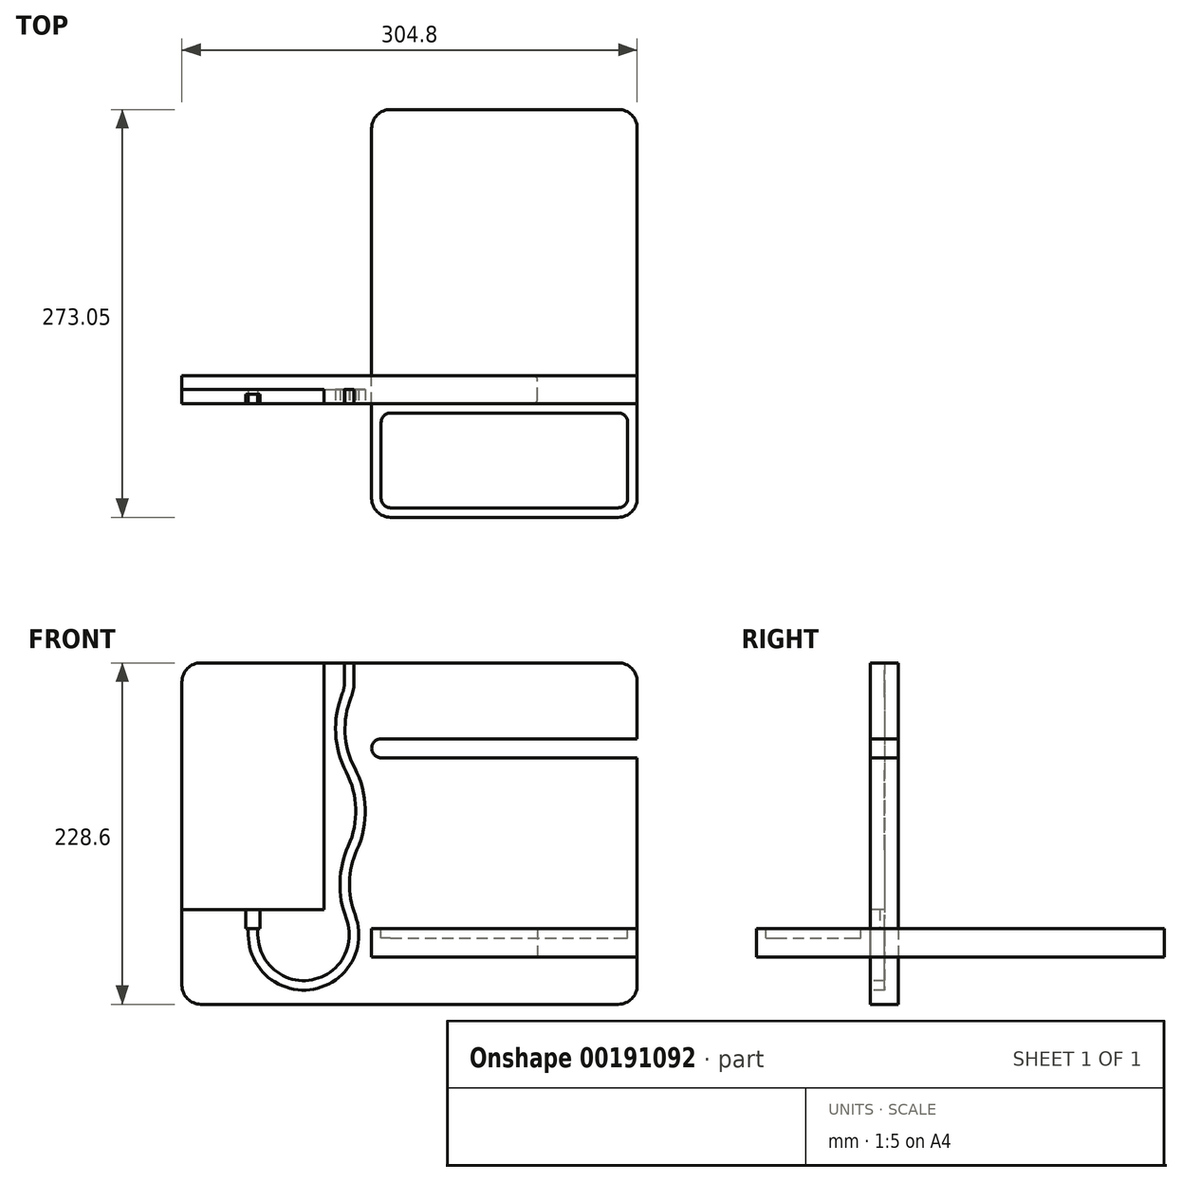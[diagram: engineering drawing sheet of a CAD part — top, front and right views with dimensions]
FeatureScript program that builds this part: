
annotation { "Feature Type Name" : "Feature", "Feature Type Description" : "" }
export const myFeature = defineFeature(function(context is Context, id is Id, definition is map)
    precondition{}
    {
        {
            var Q0;
            Q0=qCreatedBy(makeId("Front.planeOp"),FACE);
            var sketch = newSketch(context, id + "F0", { "sketchPlane" : qUnion([Q0])});
            skLineSegment(sketch, "E0.bottom", {"start": v(-152.4, 114.3) * mm, "end": v(152.4, 114.3) * mm});
            skLineSegment(sketch, "E0.top", {"start": v(-152.4, -114.3) * mm, "end": v(152.4, -114.3) * mm});
            skLineSegment(sketch, "E0.left", {"start": v(-152.4, 114.3) * mm, "end": v(-152.4, -114.3) * mm});
            skLineSegment(sketch, "E0.right", {"start": v(152.4, 114.3) * mm, "end": v(152.4, -114.3) * mm});
            skLineSegment(sketch, "E1", {"start": v(-152.4, 114.3) * mm, "end": v(152.4, -114.3) * mm, "construction": true});
            skSolve(sketch);
        }
        {
            var Q0;
            Q0 = qSketchRegion(id + "F0", true);
            extrude(context, id + "F1", {"entities" : qUnion([Q0]), "oppositeDirection" : true, "depth" : 18.54 * mm});
        }
        {
            var Q0;
            Q0=makeQuery(id+"F1.opExtrude","CAP_FACE",FACE,{"disambiguationData":[OSD([sQuery(id+"F0.wireOp",EDGE,"E0.bottom"),sQuery(id+"F0.wireOp",EDGE,"E0.top"),sQuery(id+"F0.wireOp",EDGE,"E0.left"),sQuery(id+"F0.wireOp",EDGE,"E0.right")])],"isStart":true});
            var sketch = newSketch(context, id + "F2", { "sketchPlane" : qUnion([Q0])});
            skLineSegment(sketch, "E2.bottom", {"start": v(-25.4, 63.5) * mm, "end": v(152.4, 63.5) * mm});
            skLineSegment(sketch, "E2.top", {"start": v(-25.4, 50.8) * mm, "end": v(152.4, 50.8) * mm});
            skLineSegment(sketch, "E2.left", {"start": v(-25.4, 63.5) * mm, "end": v(-25.4, 50.8) * mm});
            skLineSegment(sketch, "E2.right", {"start": v(152.4, 63.5) * mm, "end": v(152.4, 50.8) * mm});
            skLineSegment(sketch, "E3.bottom", {"start": v(152.4, -63.5) * mm, "end": v(76.2, -63.5) * mm});
            skLineSegment(sketch, "E3.top", {"start": v(152.4, -82.55) * mm, "end": v(76.2, -82.55) * mm});
            skLineSegment(sketch, "E3.left", {"start": v(152.4, -63.5) * mm, "end": v(152.4, -82.55) * mm});
            skLineSegment(sketch, "E3.right", {"start": v(76.2, -63.5) * mm, "end": v(76.2, -82.55) * mm});
            skSolve(sketch);
        }
        {
            var Q0;
            Q0 = qSketchRegion(id + "F2", true);
            extrude(context, id + "F3", {"entities" : qUnion([Q0]), "operationType" : NewBodyOperationType.REMOVE, "endBound" : BoundingType.THROUGH_ALL, "oppositeDirection" : true, "depth" : 25.4 * mm});
        }
        {
            var Q0;
            Q0=makeQuery(id+"F1.opExtrude","CAP_FACE",FACE,{"disambiguationData":[OSD([sQuery(id+"F0.wireOp",EDGE,"E0.bottom"),sQuery(id+"F0.wireOp",EDGE,"E0.top"),sQuery(id+"F0.wireOp",EDGE,"E0.left"),sQuery(id+"F0.wireOp",EDGE,"E0.right")])],"isStart":true});
            var sketch = newSketch(context, id + "F4", { "sketchPlane" : qUnion([Q0])});
            skLineSegment(sketch, "E4.bottom", {"start": v(-152.4, 114.3) * mm, "end": v(-57.15, 114.3) * mm});
            skLineSegment(sketch, "E4.top", {"start": v(-152.4, -50.8) * mm, "end": v(-57.15, -50.8) * mm});
            skLineSegment(sketch, "E4.left", {"start": v(-152.4, 114.3) * mm, "end": v(-152.4, -50.8) * mm});
            skLineSegment(sketch, "E4.right", {"start": v(-57.15, 114.3) * mm, "end": v(-57.15, -50.8) * mm});
            skSolve(sketch);
        }
        {
            var Q0;
            Q0 = qSketchRegion(id + "F4", true);
            extrude(context, id + "F5", {"entities" : qUnion([Q0]), "operationType" : NewBodyOperationType.REMOVE, "oppositeDirection" : true, "depth" : 9.52 * mm});
        }
        {
            var Q0;
            Q0=makeQuery(id+"F1.opExtrude","CAP_FACE",FACE,{"disambiguationData":[OSD([sQuery(id+"F0.wireOp",EDGE,"E0.bottom"),sQuery(id+"F0.wireOp",EDGE,"E0.top"),sQuery(id+"F0.wireOp",EDGE,"E0.left"),sQuery(id+"F0.wireOp",EDGE,"E0.right")])],"isStart":true});
            var sketch = newSketch(context, id + "F6", { "sketchPlane" : qUnion([Q0])});
            skLineSegment(sketch, "E5", {"start": v(-104.78, -50.8) * mm, "end": v(-104.78, -63.5) * mm, "construction": true});
            skPoint(sketch, "E5.endSnap0", {"position": v(-104.78, -50.8) * mm});
            skLineSegment(sketch, "E6.bottom", {"start": v(-109.54, -50.8) * mm, "end": v(-100.01, -50.8) * mm});
            skLineSegment(sketch, "E6.top", {"start": v(-109.54, -63.5) * mm, "end": v(-100.01, -63.5) * mm});
            skLineSegment(sketch, "E6.left", {"start": v(-109.54, -50.8) * mm, "end": v(-109.54, -63.5) * mm});
            skLineSegment(sketch, "E6.right", {"start": v(-100.01, -50.8) * mm, "end": v(-100.01, -63.5) * mm});
            skSolve(sketch);
        }
        {
            var Q0;
            Q0 = qSketchRegion(id + "F6", true);
            extrude(context, id + "F7", {"entities" : qUnion([Q0]), "operationType" : NewBodyOperationType.REMOVE, "oppositeDirection" : true, "depth" : 6.35 * mm});
        }
        {
            var Q0;
            Q0=makeQuery(id+"F1.opExtrude","CAP_FACE",FACE,{"disambiguationData":[OSD([sQuery(id+"F0.wireOp",EDGE,"E0.bottom"),sQuery(id+"F0.wireOp",EDGE,"E0.top"),sQuery(id+"F0.wireOp",EDGE,"E0.left"),sQuery(id+"F0.wireOp",EDGE,"E0.right")])],"isStart":true});
            var sketch = newSketch(context, id + "F8", { "sketchPlane" : qUnion([Q0])});
            skLineSegment(sketch, "E7", {"start": v(-104.78, -63.5) * mm, "end": v(-104.78, -67.81) * mm, "construction": true});
            skPoint(sketch, "E7.endSnap0", {"position": v(-104.78, -63.5) * mm});
            skArc(sketch, "E8", {"start": v(-104.77, -67.81) * mm, "mid": v(-64.8, -101.04) * mm, "end": v(-39.44, -55.66) * mm, "construction": true});
            skLineSegment(sketch, "E9", {"start": v(-104.77, -67.81) * mm, "end": v(-37.18, -67.81) * mm, "construction": true});
            skLineSegment(sketch, "E10", {"start": v(-70.98, -67.81) * mm, "end": v(-9.16, -43.98) * mm, "construction": true});
            skArc(sketch, "E11", {"start": v(-39.44, -55.66) * mm, "mid": v(-43.41, -32.5) * mm, "end": v(-38.14, -9.61) * mm, "construction": true});
            skArc(sketch, "E12", {"start": v(-38.14, -9.61) * mm, "mid": v(-32.87, 16.67) * mm, "end": v(-39.63, 42.6) * mm, "construction": true});
            skArc(sketch, "E13", {"start": v(-39.63, 42.6) * mm, "mid": v(-46.34, 67.23) * mm, "end": v(-42.15, 92.4) * mm, "construction": true});
            skLineSegment(sketch, "E14", {"start": v(-40.33, 101.84) * mm, "end": v(-40.33, 114.3) * mm, "construction": true});
            skPoint(sketch, "E15.visualSharp", {"position": v(-40.33, 96.5) * mm});
            skArc(sketch, "E15.filletArc", {"start": v(-42.15, 92.4) * mm, "mid": v(-40.79, 97.04) * mm, "end": v(-40.33, 101.84) * mm, "construction": true});
            skLineSegment(sketch, "E16.0", {"start": v(-37.16, 101.84) * mm, "end": v(-37.16, 114.3) * mm});
            skArc(sketch, "E16.1", {"start": v(-39.2, 91.23) * mm, "mid": v(-37.67, 96.44) * mm, "end": v(-37.16, 101.84) * mm});
            skArc(sketch, "E16.2", {"start": v(-36.82, 44.07) * mm, "mid": v(-43.17, 67.4) * mm, "end": v(-39.2, 91.23) * mm});
            skLineSegment(sketch, "E16.3", {"start": v(-107.95, -63.5) * mm, "end": v(-107.95, -67.81) * mm});
            skArc(sketch, "E16.4", {"start": v(-107.95, -67.81) * mm, "mid": v(-64.21, -104.16) * mm, "end": v(-36.48, -54.51) * mm});
            skArc(sketch, "E16.5", {"start": v(-36.48, -54.51) * mm, "mid": v(-40.24, -32.6) * mm, "end": v(-35.25, -10.92) * mm});
            skArc(sketch, "E16.6", {"start": v(-35.25, -10.92) * mm, "mid": v(-29.7, 16.76) * mm, "end": v(-36.82, 44.07) * mm});
            skLineSegment(sketch, "E17.0", {"start": v(-43.5, 101.84) * mm, "end": v(-43.5, 114.3) * mm});
            skArc(sketch, "E17.1", {"start": v(-45.1, 93.59) * mm, "mid": v(-43.9, 97.64) * mm, "end": v(-43.5, 101.84) * mm});
            skArc(sketch, "E17.2", {"start": v(-42.44, 41.13) * mm, "mid": v(-49.51, 67.07) * mm, "end": v(-45.1, 93.59) * mm});
            skLineSegment(sketch, "E17.3", {"start": v(-101.6, -63.5) * mm, "end": v(-101.6, -67.81) * mm});
            skArc(sketch, "E17.4", {"start": v(-101.6, -67.81) * mm, "mid": v(-65.38, -97.92) * mm, "end": v(-42.4, -56.8) * mm});
            skArc(sketch, "E17.5", {"start": v(-42.4, -56.8) * mm, "mid": v(-46.59, -32.41) * mm, "end": v(-41.03, -8.3) * mm});
            skArc(sketch, "E17.6", {"start": v(-41.03, -8.3) * mm, "mid": v(-36.04, 16.58) * mm, "end": v(-42.44, 41.13) * mm});
            skLineSegment(sketch, "E18", {"start": v(-43.5, 114.3) * mm, "end": v(-37.16, 114.3) * mm});
            skLineSegment(sketch, "E19", {"start": v(-107.95, -63.5) * mm, "end": v(-101.6, -63.5) * mm});
            skSolve(sketch);
        }
        {
            var Q0;
            Q0 = qSketchRegion(id + "F8", true);
            extrude(context, id + "F9", {"entities" : qUnion([Q0]), "operationType" : NewBodyOperationType.REMOVE, "oppositeDirection" : true, "depth" : 9.52 * mm});
        }
        {
            var Q0;
            Q0=makeQuery(id+"F1.opExtrude","SWEPT_EDGE",EDGE,{"disambiguationData":[OSD([sQuery(id+"F0.wireOp",EDGE,"E0.bottom"),sQuery(id+"F0.wireOp",EDGE,"E0.right")])]});
            var Q1;
            Q1=makeQuery(id+"F1.opExtrude","SWEPT_EDGE",EDGE,{"disambiguationData":[OSD([sQuery(id+"F0.wireOp",EDGE,"E0.top"),sQuery(id+"F0.wireOp",EDGE,"E0.right")])]});
            var Q2;
            Q2=makeQuery(id+"F1.opExtrude","SWEPT_EDGE",EDGE,{"disambiguationData":[OSD([sQuery(id+"F0.wireOp",EDGE,"E0.bottom"),sQuery(id+"F0.wireOp",EDGE,"E0.left")])]});
            var Q3;
            Q3=makeQuery(id+"F1.opExtrude","SWEPT_EDGE",EDGE,{"disambiguationData":[OSD([sQuery(id+"F0.wireOp",EDGE,"E0.top"),sQuery(id+"F0.wireOp",EDGE,"E0.left")])]});
            fillet(context, id + "F10", {"entities" : qUnion([Q0, Q1, Q2, Q3]), "radius" : 12.7 * mm, "tangentPropagation" : true, "allowEdgeOverflow" : false});
        }
        {
            var Q0;
            Q0=makeQuery(id+"F3.boolean.opBoolean","COPY",EDGE,{"derivedFrom":makeQuery(id+"F3.opExtrude","SWEPT_EDGE",EDGE,{"disambiguationData":[OSD([sQuery(id+"F2.wireOp",EDGE,"E2.bottom"),sQuery(id+"F2.wireOp",EDGE,"E2.left")])]})});
            var Q1;
            Q1=makeQuery(id+"F3.boolean.opBoolean","COPY",EDGE,{"derivedFrom":makeQuery(id+"F3.opExtrude","SWEPT_EDGE",EDGE,{"disambiguationData":[OSD([sQuery(id+"F2.wireOp",EDGE,"E2.top"),sQuery(id+"F2.wireOp",EDGE,"E2.left")])]})});
            var Q2;
            Q2=makeQuery(id+"F3.boolean.opBoolean","COPY",EDGE,{"derivedFrom":makeQuery(id+"F3.opExtrude","SWEPT_EDGE",EDGE,{"disambiguationData":[OSD([sQuery(id+"F2.wireOp",EDGE,"E3.top"),sQuery(id+"F2.wireOp",EDGE,"E3.right")])]})});
            var Q3;
            Q3=makeQuery(id+"F3.boolean.opBoolean","COPY",EDGE,{"derivedFrom":makeQuery(id+"F3.opExtrude","SWEPT_EDGE",EDGE,{"disambiguationData":[OSD([sQuery(id+"F2.wireOp",EDGE,"E3.bottom"),sQuery(id+"F2.wireOp",EDGE,"E3.right")])]})});
            fillet(context, id + "F11", {"entities" : qUnion([Q0, Q1, Q2, Q3]), "radius" : 6.35 * mm, "tangentPropagation" : true, "allowEdgeOverflow" : false});
        }
        {
            var Q0;
            Q0=qCreatedBy(makeId("Right.planeOp"),FACE);
            var sketch = newSketch(context, id + "F12", { "sketchPlane" : qUnion([Q0])});
            skLineSegment(sketch, "E20.bottom", {"start": v(-76.2, -63.5) * mm, "end": v(196.85, -63.5) * mm});
            skLineSegment(sketch, "E20.top", {"start": v(-76.2, -82.55) * mm, "end": v(196.85, -82.55) * mm});
            skLineSegment(sketch, "E20.left", {"start": v(-76.2, -63.5) * mm, "end": v(-76.2, -82.55) * mm});
            skLineSegment(sketch, "E20.right", {"start": v(196.85, -63.5) * mm, "end": v(196.85, -82.55) * mm});
            skLineSegment(sketch, "E21", {"start": v(1.53, -117.33) * mm, "end": v(222.6, -77.97) * mm, "construction": true});
            skSolve(sketch);
        }
        {
            var Q0;
            Q0 = qSketchRegion(id + "F12", true);
            var Q1;
            {var subQ0=sQuery(id+"F0.wireOp",EDGE,"E0.right");Q1=makeQuery(id+"F3.boolean.opBoolean","SPLIT",FACE,{"disambiguationData":[TD([makeQuery(id+"F3.opExtrude","SWEPT_FACE",FACE,{"disambiguationData":[OSD([sQuery(id+"F2.wireOp",EDGE,"E2.top")])]})])],"derivedFrom":makeQuery(id+"F1.opExtrude","SWEPT_FACE",FACE,{"disambiguationData":[OSD([subQ0])]})});}
            extrude(context, id + "F13", {"entities" : qUnion([Q0]), "endBound" : BoundingType.UP_TO_SURFACE, "endBoundEntityFace" : qUnion([Q1]), "depth" : 25.4 * mm, "hasSecondDirection" : true, "secondDirectionOppositeDirection" : true, "secondDirectionDepth" : 25.4 * mm});
        }
        {
            var Q0;
            Q0=makeQuery(id+"F13.opExtrude","CAP_FACE",FACE,{"disambiguationData":[OSD([sQuery(id+"F12.wireOp",EDGE,"E20.bottom"),sQuery(id+"F12.wireOp",EDGE,"E20.top"),sQuery(id+"F12.wireOp",EDGE,"E20.left"),sQuery(id+"F12.wireOp",EDGE,"E20.right")])],"isStart":true});
            var sketch = newSketch(context, id + "F14", { "sketchPlane" : qUnion([Q0])});
            skLineSegment(sketch, "E22.0", {"start": v(0, -63.5) * mm, "end": v(0, -82.55) * mm});
            skLineSegment(sketch, "E23.0", {"start": v(0, -82.55) * mm, "end": v(-18.54, -82.55) * mm});
            skLineSegment(sketch, "E24.0", {"start": v(0, -63.5) * mm, "end": v(-18.54, -63.5) * mm});
            skPoint(sketch, "E25.orphan", {"position": v(0, -63.5) * mm});
            skLineSegment(sketch, "E26.0", {"start": v(-18.54, -63.5) * mm, "end": v(-18.54, -82.55) * mm});
            skPoint(sketch, "E27.orphan", {"position": v(-18.54, -63.5) * mm});
            skPoint(sketch, "E28.orphan", {"position": v(-18.54, 50.8) * mm});
            skPoint(sketch, "E29.orphan", {"position": v(0, 50.8) * mm});
            skPoint(sketch, "E30.orphan", {"position": v(-196.85, -63.5) * mm});
            skPoint(sketch, "E31.orphan", {"position": v(-196.85, -82.55) * mm});
            skPoint(sketch, "E32.orphan", {"position": v(76.2, -82.55) * mm});
            skPoint(sketch, "E33.orphan", {"position": v(76.2, -63.5) * mm});
            skSolve(sketch);
        }
        {
            var Q0;
            Q0 = qSketchRegion(id + "F14", true);
            extrude(context, id + "F15", {"entities" : qUnion([Q0]), "operationType" : NewBodyOperationType.REMOVE, "oppositeDirection" : true, "depth" : 111.12 * mm});
        }
        {
            var Q0;
            Q0=makeQuery(id+"F13.opExtrude","CAP_EDGE",EDGE,{"disambiguationData":[OSD([sQuery(id+"F12.wireOp",EDGE,"E20.left")])],"isStart":true});
            var Q1;
            Q1=makeQuery(id+"F13.opExtrude","CAP_EDGE",EDGE,{"disambiguationData":[OSD([sQuery(id+"F12.wireOp",EDGE,"E20.left")])],"isStart":false});
            var Q2;
            Q2=makeQuery(id+"F13.opExtrude","CAP_EDGE",EDGE,{"disambiguationData":[OSD([sQuery(id+"F12.wireOp",EDGE,"E20.right")])],"isStart":false});
            var Q3;
            Q3=makeQuery(id+"F13.opExtrude","CAP_EDGE",EDGE,{"disambiguationData":[OSD([sQuery(id+"F12.wireOp",EDGE,"E20.right")])],"isStart":true});
            fillet(context, id + "F16", {"entities" : qUnion([Q0, Q1, Q2, Q3]), "radius" : 12.7 * mm, "tangentPropagation" : true, "allowEdgeOverflow" : false});
        }
        {
            var Q0;
            Q0=makeQuery(id+"F15.boolean.opBoolean","COPY",EDGE,{"derivedFrom":makeQuery(id+"F15.opExtrude","CAP_EDGE",EDGE,{"disambiguationData":[OSD([sQuery(id+"F14.wireOp",EDGE,"E26.0")])],"isStart":false})});
            var Q1;
            Q1=makeQuery(id+"F15.boolean.opBoolean","COPY",EDGE,{"derivedFrom":makeQuery(id+"F15.opExtrude","CAP_EDGE",EDGE,{"disambiguationData":[OSD([sQuery(id+"F14.wireOp",EDGE,"E22.0")])],"isStart":false})});
            fillet(context, id + "F17", {"entities" : qUnion([Q0, Q1]), "radius" : 3.17 * mm, "tangentPropagation" : true, "allowEdgeOverflow" : false});
        }
        {
            var Q0;
            Q0=makeQuery(id+"F13.opExtrude","SWEPT_FACE",FACE,{"disambiguationData":[OSD([sQuery(id+"F12.wireOp",EDGE,"E20.bottom")])]});
            var sketch = newSketch(context, id + "F18", { "sketchPlane" : qUnion([Q0])});
            skLineSegment(sketch, "E34.bottom", {"start": v(-19.05, -69.85) * mm, "end": v(146.05, -69.85) * mm});
            skLineSegment(sketch, "E34.top", {"start": v(-19.05, -6.35) * mm, "end": v(146.05, -6.35) * mm});
            skLineSegment(sketch, "E34.left", {"start": v(-19.05, -69.85) * mm, "end": v(-19.05, -6.35) * mm});
            skLineSegment(sketch, "E34.right", {"start": v(146.05, -69.85) * mm, "end": v(146.05, -6.35) * mm});
            skSolve(sketch);
        }
        {
            var Q0;
            Q0 = qSketchRegion(id + "F18", true);
            extrude(context, id + "F19", {"entities" : qUnion([Q0]), "operationType" : NewBodyOperationType.REMOVE, "oppositeDirection" : true, "depth" : 6.35 * mm});
        }
        {
            var Q0;
            Q0=makeQuery(id+"F19.boolean.opBoolean","COPY",EDGE,{"derivedFrom":makeQuery(id+"F19.opExtrude","SWEPT_EDGE",EDGE,{"disambiguationData":[OSD([sQuery(id+"F18.wireOp",EDGE,"E34.bottom"),sQuery(id+"F18.wireOp",EDGE,"E34.left")])]})});
            var Q1;
            Q1=makeQuery(id+"F19.boolean.opBoolean","COPY",EDGE,{"derivedFrom":makeQuery(id+"F19.opExtrude","SWEPT_EDGE",EDGE,{"disambiguationData":[OSD([sQuery(id+"F18.wireOp",EDGE,"E34.top"),sQuery(id+"F18.wireOp",EDGE,"E34.left")])]})});
            var Q2;
            Q2=makeQuery(id+"F19.boolean.opBoolean","COPY",EDGE,{"derivedFrom":makeQuery(id+"F19.opExtrude","SWEPT_EDGE",EDGE,{"disambiguationData":[OSD([sQuery(id+"F18.wireOp",EDGE,"E34.top"),sQuery(id+"F18.wireOp",EDGE,"E34.right")])]})});
            var Q3;
            Q3=makeQuery(id+"F19.boolean.opBoolean","COPY",EDGE,{"derivedFrom":makeQuery(id+"F19.opExtrude","SWEPT_EDGE",EDGE,{"disambiguationData":[OSD([sQuery(id+"F18.wireOp",EDGE,"E34.bottom"),sQuery(id+"F18.wireOp",EDGE,"E34.right")])]})});
            fillet(context, id + "F20", {"entities" : qUnion([Q0, Q1, Q2, Q3]), "radius" : 6.35 * mm, "tangentPropagation" : true, "allowEdgeOverflow" : false});
        }
    });
